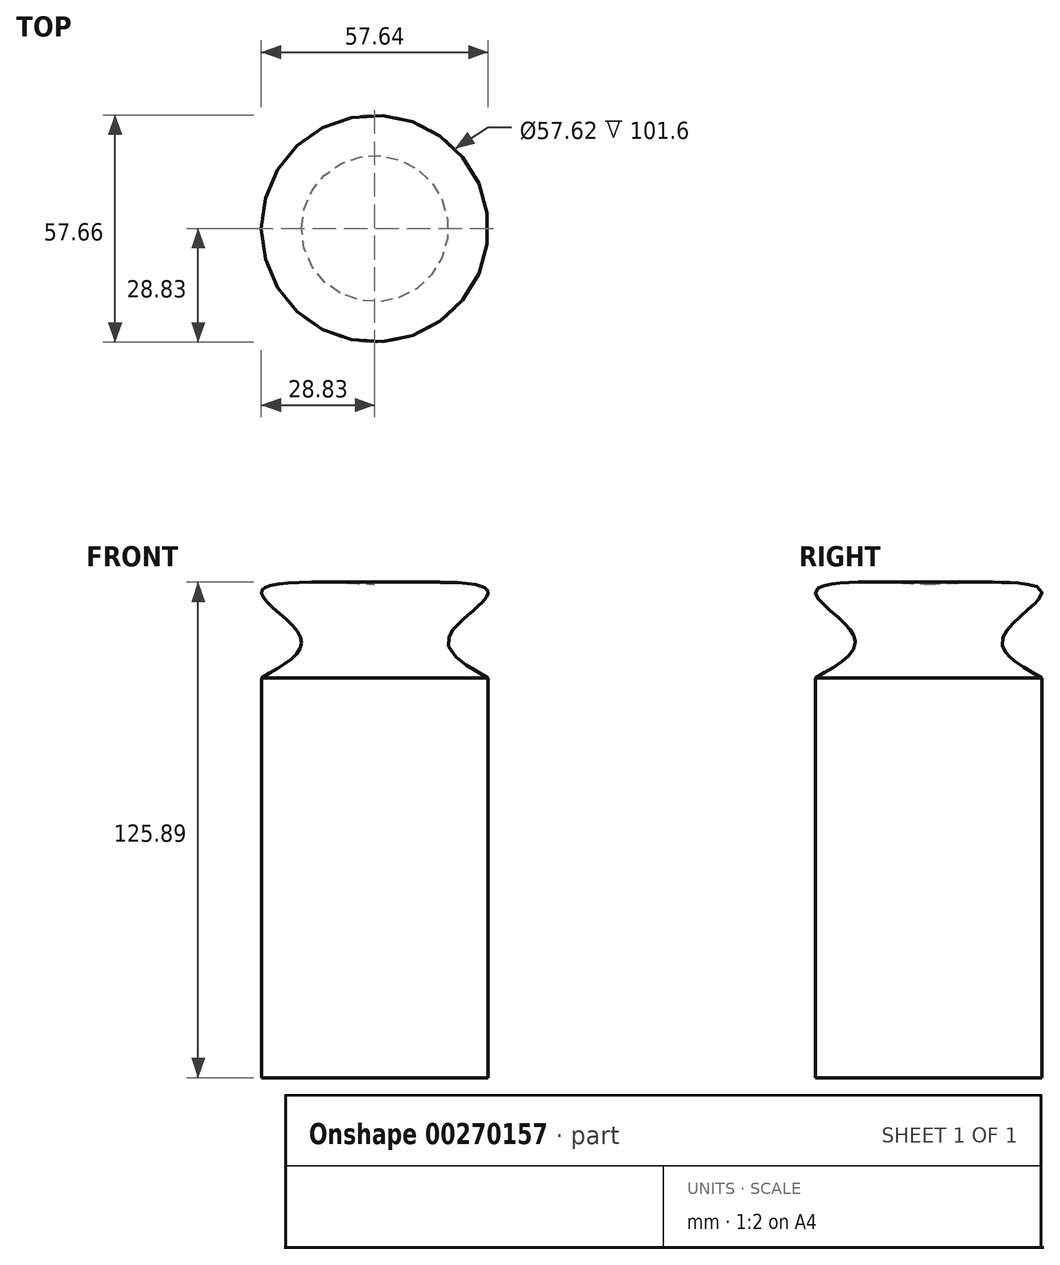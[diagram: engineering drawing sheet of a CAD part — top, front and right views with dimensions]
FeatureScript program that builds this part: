
annotation { "Feature Type Name" : "Feature", "Feature Type Description" : "" }
export const myFeature = defineFeature(function(context is Context, id is Id, definition is map)
    precondition{}
    {
        {
            var Q0;
            Q0=qCreatedBy(makeId("Front.planeOp"),FACE);
            var sketch = newSketch(context, id + "F0", { "sketchPlane" : qUnion([Q0])});
            skLineSegment(sketch, "E0", {"start": v(-28.81, -75.93) * mm, "end": v(-28.81, 25.67) * mm});
            skFitSpline(sketch, "E1", {"points": [v(-28.81, 25.67) * mm, v(-18.76, 35.75) * mm, v(-28.81, 47.14) * mm, v(0, 49.49) * mm], "startDerivative": vector(58.18, 32.23) * mm, "endDerivative": vector(106.95, -4.5) * mm});
            skLineSegment(sketch, "E2", {"start": v(-28.81, -75.93) * mm, "end": v(0, -75.93) * mm});
            skSolve(sketch);
        }
        {
            var Q0;
            Q0=qCreatedBy(makeId("Front.planeOp"),FACE);
            var sketch = newSketch(context, id + "F1", { "sketchPlane" : qUnion([Q0])});
            skLineSegment(sketch, "E3", {"start": v(0, -75.23) * mm, "end": v(0, 0) * mm, "construction": true});
            skSolve(sketch);
        }
        {
            var Q0;
            Q0=sQuery(id+"F0.wireOp",EDGE,"E1");
            var Q1;
            Q1=sQuery(id+"F0.wireOp",EDGE,"E0");
            var Q2;
            Q2=sQuery(id+"F0.wireOp",EDGE,"E2");
            var Q3;
            Q3=sQuery(id+"F1.wireOp",EDGE,"E3");
            revolve(context, id + "F2", {"bodyType" : ToolBodyType.SURFACE, "surfaceEntities" : qUnion([Q0, Q1, Q2]), "axis" : qUnion([Q3]), "revolveType" : RevolveType.FULL});
        }
    });
